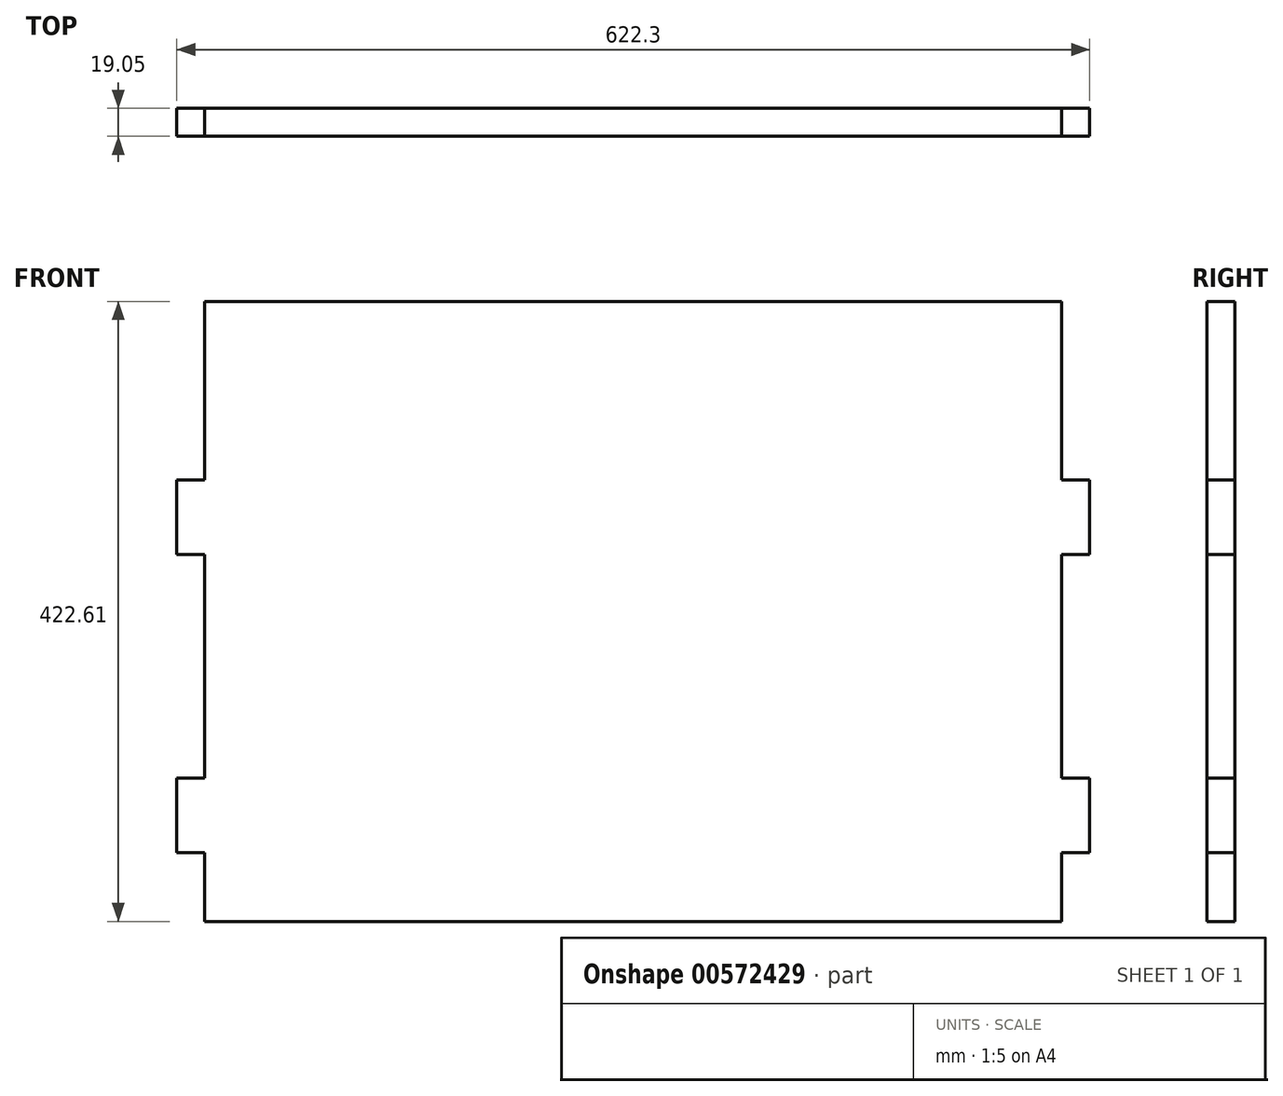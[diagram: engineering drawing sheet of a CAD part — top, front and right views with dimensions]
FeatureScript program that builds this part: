
annotation { "Feature Type Name" : "Feature", "Feature Type Description" : "" }
export const myFeature = defineFeature(function(context is Context, id is Id, definition is map)
    precondition{}
    {
        {
            var Q0;
            Q0=qCreatedBy(makeId("Front.planeOp"),FACE);
            var sketch = newSketch(context, id + "F0", { "sketchPlane" : qUnion([Q0])});
            skLineSegment(sketch, "E0.bottom", {"start": v(0, 0) * mm, "end": v(584.2, 0) * mm});
            skLineSegment(sketch, "E0.top", {"start": v(0, 347.98) * mm, "end": v(584.2, 347.98) * mm});
            skLineSegment(sketch, "E0.left", {"start": v(0, 0) * mm, "end": v(0, 46.99) * mm});
            skLineSegment(sketch, "E0.right", {"start": v(584.2, 0) * mm, "end": v(584.2, 46.99) * mm});
            skLineSegment(sketch, "E1", {"start": v(292.1, 347.98) * mm, "end": v(292.1, -296.1) * mm, "construction": true});
            skLineSegment(sketch, "E2", {"start": v(0, 174) * mm, "end": v(768.38, 174) * mm, "construction": true});
            skLineSegment(sketch, "E3.bottom", {"start": v(0, 301) * mm, "end": v(-19.05, 301) * mm});
            skLineSegment(sketch, "E3.top", {"start": v(0, 250.2) * mm, "end": v(-19.05, 250.2) * mm});
            skLineSegment(sketch, "E3.right", {"start": v(-19.05, 301) * mm, "end": v(-19.05, 250.2) * mm});
            skLineSegment(sketch, "E4.MirrorCS", {"start": v(0, 46.99) * mm, "end": v(-19.05, 46.99) * mm});
            skLineSegment(sketch, "E5.MirrorCS", {"start": v(-19.05, 46.99) * mm, "end": v(-19.05, 97.79) * mm});
            skLineSegment(sketch, "E6.MirrorCS", {"start": v(0, 97.79) * mm, "end": v(-19.05, 97.79) * mm});
            skLineSegment(sketch, "E7.MirrorCS", {"start": v(584.2, 301) * mm, "end": v(603.25, 301) * mm});
            skLineSegment(sketch, "E8.MirrorCS", {"start": v(603.25, 301) * mm, "end": v(603.25, 250.2) * mm});
            skLineSegment(sketch, "E9.MirrorCS", {"start": v(584.2, 250.2) * mm, "end": v(603.25, 250.2) * mm});
            skLineSegment(sketch, "E10.MirrorCS", {"start": v(584.2, 97.79) * mm, "end": v(603.25, 97.79) * mm});
            skLineSegment(sketch, "E11.MirrorCS", {"start": v(603.25, 46.99) * mm, "end": v(603.25, 97.79) * mm});
            skLineSegment(sketch, "E12.MirrorCS", {"start": v(584.2, 46.99) * mm, "end": v(603.25, 46.99) * mm});
            skLineSegment(sketch, "E13.trimOffspring", {"start": v(0, 301) * mm, "end": v(0, 347.98) * mm});
            skPoint(sketch, "E14.MirrorCS.end.orphan", {"position": v(0, 97.79) * mm});
            skPoint(sketch, "E14.MirrorCS.start.orphan", {"position": v(0, 46.99) * mm});
            skLineSegment(sketch, "E15.trimOffspring", {"start": v(0, 97.79) * mm, "end": v(0, 250.2) * mm});
            skLineSegment(sketch, "E16.trimOffspring", {"start": v(584.2, 97.79) * mm, "end": v(584.2, 250.2) * mm});
            skLineSegment(sketch, "E17.trimOffspring", {"start": v(584.2, 301) * mm, "end": v(584.2, 347.98) * mm});
            skLineSegment(sketch, "E18", {"start": v(0, 347.98) * mm, "end": v(0, 422.61) * mm});
            skLineSegment(sketch, "E19", {"start": v(584.2, 347.98) * mm, "end": v(584.2, 422.61) * mm});
            skLineSegment(sketch, "E20", {"start": v(0, 422.61) * mm, "end": v(584.2, 422.61) * mm});
            skSolve(sketch);
        }
        {
            var Q0;
            Q0 = qSketchRegion(id + "F0", true);
            extrude(context, id + "F1", {"entities" : qUnion([Q0]), "depth" : 19.05 * mm, "offsetDistance" : 25.4 * mm});
        }
    });
